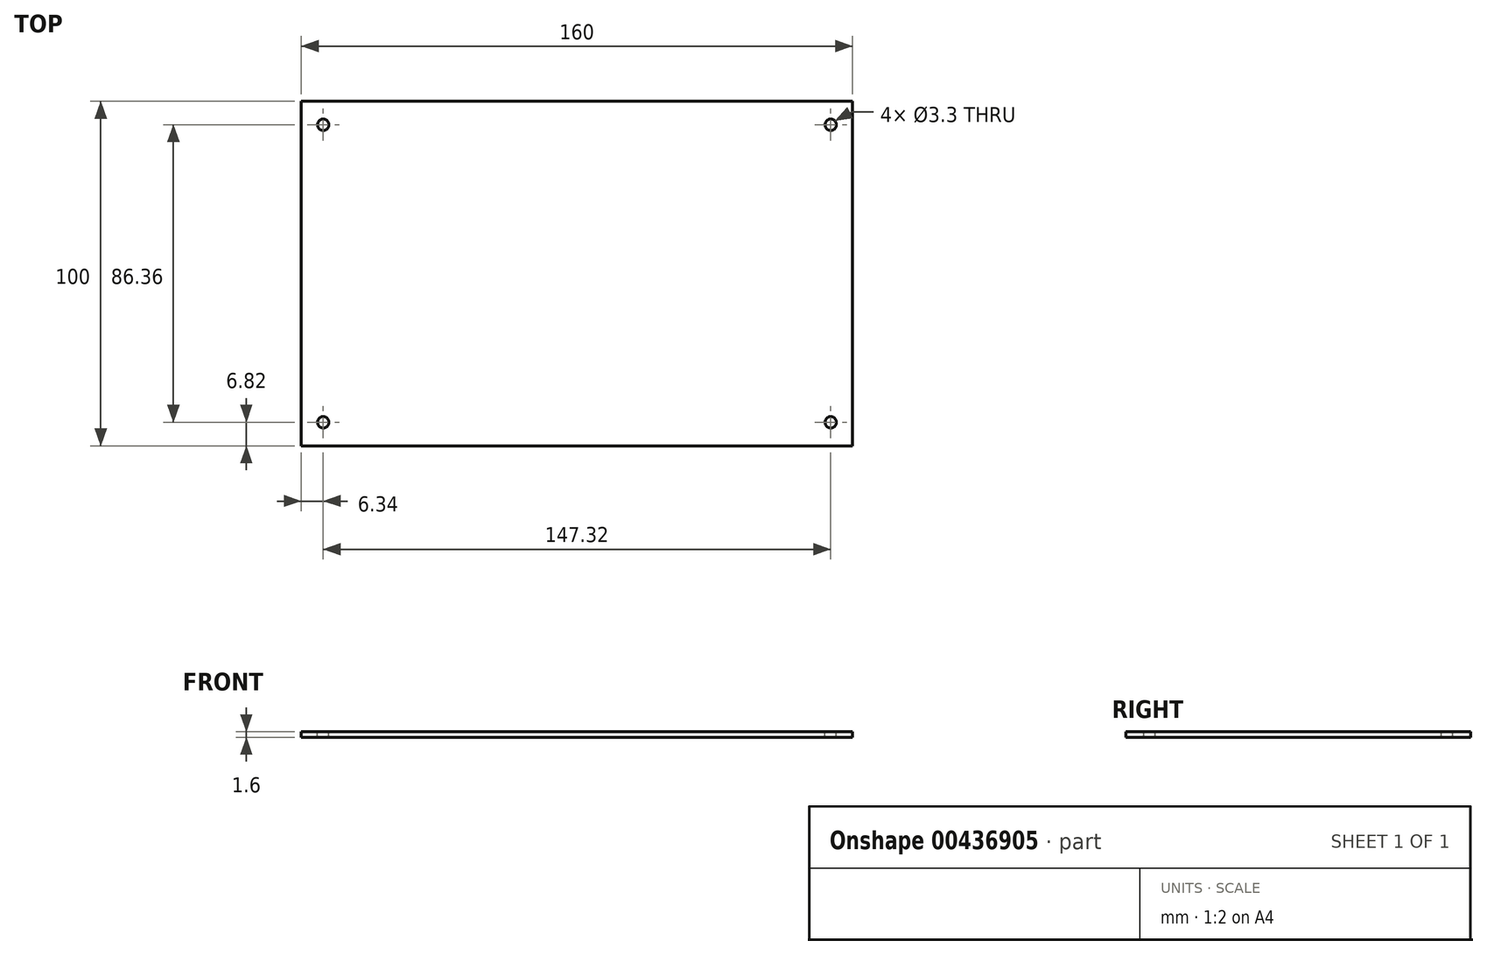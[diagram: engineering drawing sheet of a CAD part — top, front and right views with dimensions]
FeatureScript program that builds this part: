
annotation { "Feature Type Name" : "Feature", "Feature Type Description" : "" }
export const myFeature = defineFeature(function(context is Context, id is Id, definition is map)
    precondition{}
    {
        {
            var Q0;
            Q0=qCreatedBy(makeId("Top.planeOp"),FACE);
            var sketch = newSketch(context, id + "F0", { "sketchPlane" : qUnion([Q0])});
            skLineSegment(sketch, "E0.bottom", {"start": v(0, 0) * mm, "end": v(160, 0) * mm});
            skLineSegment(sketch, "E0.top", {"start": v(0, 100) * mm, "end": v(160, 100) * mm});
            skLineSegment(sketch, "E0.left", {"start": v(0, 0) * mm, "end": v(0, 100) * mm});
            skLineSegment(sketch, "E0.right", {"start": v(160, 0) * mm, "end": v(160, 100) * mm});
            skSolve(sketch);
        }
        {
            var Q0;
            Q0 = qSketchRegion(id + "F0", true);
            extrude(context, id + "F1", {"entities" : qUnion([Q0]), "depth" : 1.6 * mm});
        }
        {
            var Q0;
            Q0=makeQuery(id+"F1.opExtrude","CAP_FACE",FACE,{"disambiguationData":[OSD([sQuery(id+"F0.wireOp",EDGE,"E0.bottom"),sQuery(id+"F0.wireOp",EDGE,"E0.top"),sQuery(id+"F0.wireOp",EDGE,"E0.left"),sQuery(id+"F0.wireOp",EDGE,"E0.right")])],"isStart":false});
            var sketch = newSketch(context, id + "F2", { "sketchPlane" : qUnion([Q0])});
            skPoint(sketch, "E1", {"position": v(6.34, 6.82) * mm});
            skPoint(sketch, "E2.0.1.0", {"position": v(6.34, 93.18) * mm});
            skPoint(sketch, "E2.1.0.0", {"position": v(153.66, 6.82) * mm});
            skPoint(sketch, "E2.1.1.0", {"position": v(153.66, 93.18) * mm});
            skLineSegment(sketch, "E2.direction1", {"start": v(6.34, 6.82) * mm, "end": v(153.66, 6.82) * mm, "construction": true});
            skLineSegment(sketch, "E2.direction2", {"start": v(6.34, 6.82) * mm, "end": v(6.34, 93.18) * mm, "construction": true});
            skSolve(sketch);
        }
        {
            var Q0;
            Q0=sQuery(id+"F2.wireOp",VERTEX,"E2.0.1.0");
            var Q1;
            Q1=sQuery(id+"F2.wireOp",VERTEX,"E1");
            var Q2;
            Q2=sQuery(id+"F2.wireOp",VERTEX,"E2.1.0.0");
            var Q3;
            Q3=sQuery(id+"F2.wireOp",VERTEX,"E2.1.1.0");
            var Q4;
            Q4=makeQuery(id+"F1.opExtrude","SWEPT_BODY",BODY,{"disambiguationData":[OSD([sQuery(id+"F0.wireOp",EDGE,"E0.bottom"),sQuery(id+"F0.wireOp",EDGE,"E0.top"),sQuery(id+"F0.wireOp",EDGE,"E0.left"),sQuery(id+"F0.wireOp",EDGE,"E0.right")])]});
            hole(context, id + "F3", {"style" : HoleStyle.SIMPLE, "endStyle" : HoleEndStyle.THROUGH, "standardTappedOrClearance" : lookupTablePath({ "standard" : "ISO", "fit" : "Normal", "size" : "M3", "type" : "Clearance" }), "standardBlindInLast" : lookupTablePath({ "fit" : "Standard", "standard" : "ISO", "size" : "M3", "type" : "Clearance" }), "holeDiameter" : 3.3 * mm, "isTappedThrough" : true, "tappedDepth" : 12 * mm, "tapClearance" : 3, "locations" : qUnion([Q0, Q1, Q2, Q3]), "scope" : qUnion([Q4])});
        }
    });
